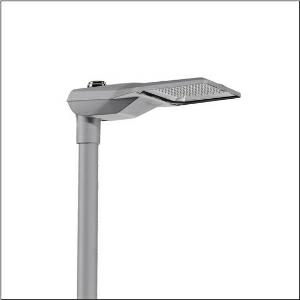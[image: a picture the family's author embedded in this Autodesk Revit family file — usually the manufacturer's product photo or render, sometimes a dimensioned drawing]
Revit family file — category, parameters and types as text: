
# Revit family: streetlight_sl_21_midi___st1_0a_5xe7d27n08nb_1197
name_source: partatom
category: Lighting Fixtures
units: mm (PartAtom-declared; Revit-internal decimal feet)

## family parameters
Cut with Voids When Loaded = No
Host = Face
Light Source = No
Part Type = Normal
Room Calculation Point = No
Round Connector Dimension = Use Diameter
Shared = No

## types (1)
- --- (1 x LED, 18780 lm, 151.2 W, 2200K)
    Apparent Load = 151 VA
    CIE Flux Codes = 40 73 97 100 100
    Color Rendering = 70
    Color Temperature = 2200K
    Default Elevation = 1800 mm
    Description = Streetlight SL 21 midi, mast luminaire, primary light control with lens, of PMMA, primary optical cover: cover, of toughened safety glass, transparent, light distribution: ST1.0a, light emission: direct distribution, primary light characteristic: asymmetric, installation type: side-entry, LED, 3G 2.5mm², High Power LED, rated luminous flux: 18.780lm, luminous efficacy: 124lm/W, light colour: 722, colour temperature: 2200K, control gear: NEMA (7pin), control: overheat protection, pre-setting: linear dimming characteristic, constant luminous flux control, time-dependent luminous flux control, flexible luminous flux parameterisation, mains connection: 220..240V, AC, 50/60Hz, connection cable pre-assembled, cable length: 12,5m, wiring characteristics: H05VV-F, start of lifetime: 151W, end of service life: 157W, reduction: 70W, luminaire housing, of diecast aluminium (EN AC-44300), powder-coated, Siteco® metallic grey (DB 702S), corrosivity category C5 mid according to DIN EN ISO 12944, multi-level sealing system, sealing non-destructively replaceable, inclination adjustable: 0°, 5°, 10°, 15°, length: 644mm, width: 335mm, height: 110mm, spigot size: 42mm (side-entry), mounting height: 4..8m, protection rating (complete): IP66, insulation class (complete): insulation class I (protective earthing), certification: CE, ENEC, ENEC+, VDE, impact resistance: IK10, permissible operating ambient temperature for outdoor applications: -40..+50°C, standard-compliant lighting for roads and squares, packaging unit: 1 piece

Light Distribution: ST1.0a
    Height = 111 mm
    Lamp = 1 x LED
    Lamp Light Flux = 18780 lm
    Lamp Power = 151.2 W
    Lamp count = 1
    Length = 644 mm
    Luminous efficacy = 124 lm/W
    Manufacturer = Siteco
    ModVariant = No
    Model = 5XE7D27N08NB
    Number of Poles = 1
    OnlyDefault = Yes
    Power Factor = 1
    Product Name = Streetlight SL 21 midi | ST1.0a
    Product group = mast luminaire | pylon top
    ProductGroupID = 6100
    Protection Class = Protection class I
    Protection Degree = IP 66
    RLX_Detail_Level = 1
    RLX_Emergency_Light_Flux = 0 lm
    RLX_Emergency_Type = 0
    RLX_Emergency_Type_DB = No
    RlxData = <blob elided: 26605 chars, md5=6b5a6835>
    Socket = socket
    Standby Power = 0 W
    System Light Flux = 18781 lm
    System Power = 151 W
    Type Comments = factory setting: luminous flux: 100 % | dim-lin: 254 | 802 mA
    Type Image = l_1294377.jpg
    URL = http://relux.com
    VarID = @adj_135204
    Voltage = 0 V
    Weight = 0.00 kg
    Width = 336 mm

## geometry (parser evidence)
native form markers: Blend x4, Sweep x13
no freeform markers — native parametric forms only
